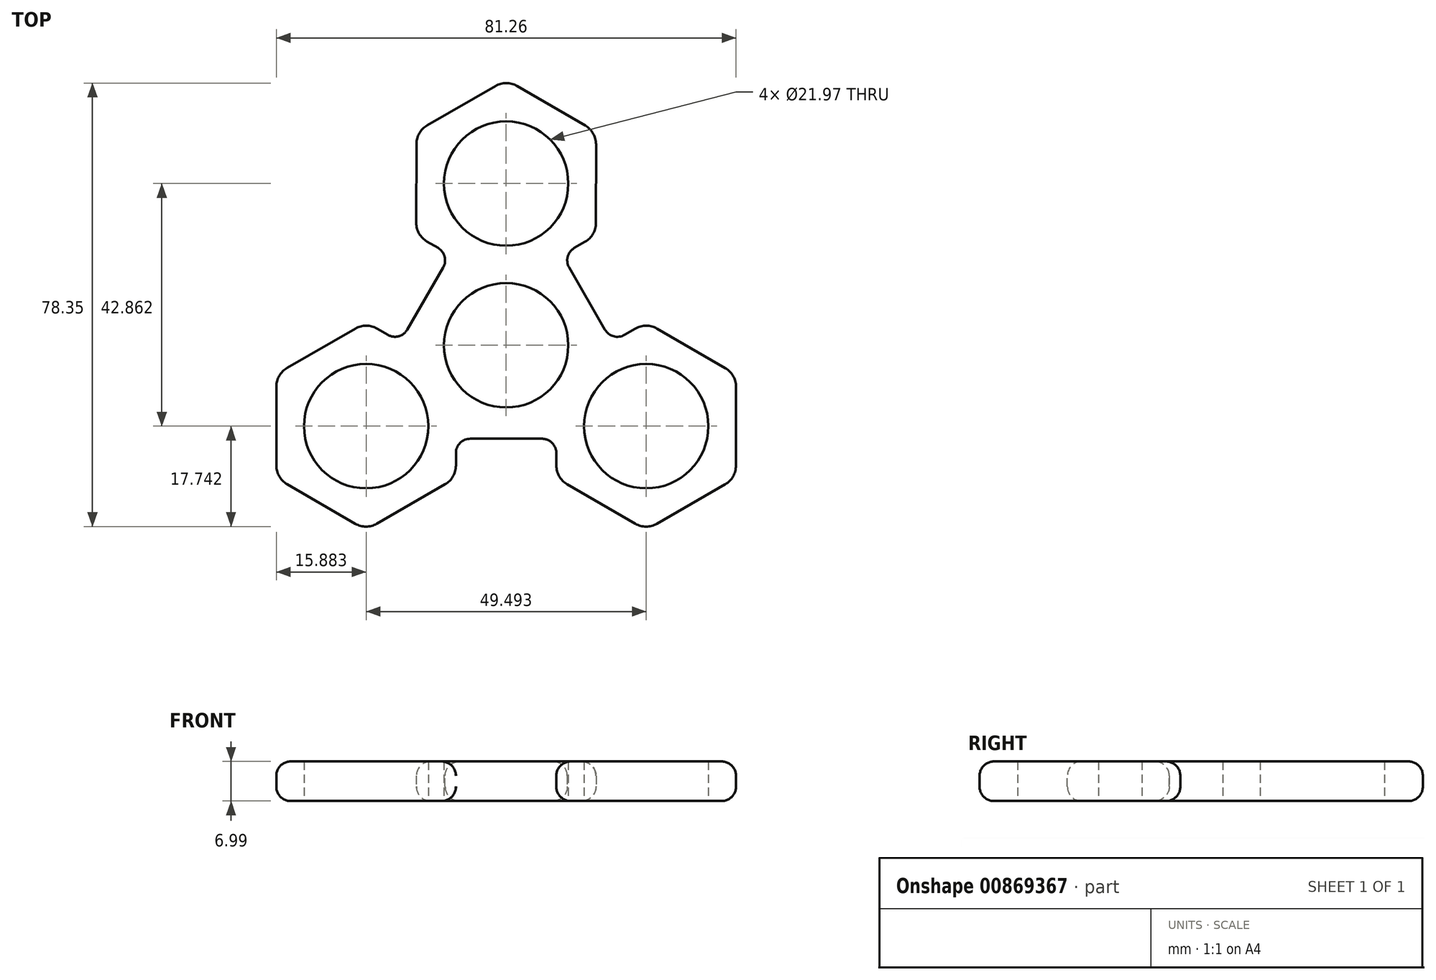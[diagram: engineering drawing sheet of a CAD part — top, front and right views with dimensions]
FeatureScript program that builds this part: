
annotation { "Feature Type Name" : "Feature", "Feature Type Description" : "" }
export const myFeature = defineFeature(function(context is Context, id is Id, definition is map)
    precondition{}
    {
        {
            var Q0;
            Q0=qCreatedBy(makeId("Top.planeOp"),FACE);
            var sketch = newSketch(context, id + "F0", { "sketchPlane" : qUnion([Q0])});
            skCircle(sketch, "E0", {"center": v(0, 0) * mm, "radius": 10.99 * mm});
            skCircle(sketch, "E1", {"center": v(0, 0) * mm, "radius": 4 * mm});
            skSolve(sketch);
        }
        {
            var Q0;
            Q0=qCreatedBy(makeId("Top.planeOp"),FACE);
            var sketch = newSketch(context, id + "F1", { "sketchPlane" : qUnion([Q0])});
            skCircle(sketch, "E2", {"center": v(0, 28.58) * mm, "radius": 10.99 * mm});
            skSolve(sketch);
        }
        {
            var Q0;
            Q0=qCreatedBy(makeId("Top.planeOp"),FACE);
            var sketch = newSketch(context, id + "F2", { "sketchPlane" : qUnion([Q0])});
            skCircle(sketch, "E3.cCircle", {"center": v(0, 28.58) * mm, "radius": 15.88 * mm, "construction": true});
            skLineSegment(sketch, "E3.0", {"start": v(-0.02, 10.24) * mm, "end": v(-15.88, 19.43) * mm});
            skLineSegment(sketch, "E3.1", {"start": v(-15.88, 19.43) * mm, "end": v(-15.87, 37.76) * mm});
            skLineSegment(sketch, "E3.2", {"start": v(-15.87, 37.76) * mm, "end": v(0.02, 46.9) * mm});
            skLineSegment(sketch, "E3.3", {"start": v(0.02, 46.9) * mm, "end": v(15.88, 37.72) * mm});
            skLineSegment(sketch, "E3.4", {"start": v(15.88, 37.72) * mm, "end": v(15.87, 19.4) * mm});
            skLineSegment(sketch, "E3.5", {"start": v(15.87, 19.4) * mm, "end": v(-0.02, 10.24) * mm});
            skPoint(sketch, "E3.0.midPoint", {"position": v(-7.95, 14.84) * mm});
            skCircle(sketch, "E4.0.0", {"center": v(0, 28.58) * mm, "radius": 10.99 * mm});
            skSolve(sketch);
        }
        {
            var Q0;
            Q0=makeQuery(id+"F1.imprint","IMPRINT",FACE,{"disambiguationData":[TD([[makeQuery(id+"F1.imprint","IMPRINT",EDGE,{"derivedFrom":sQuery(id+"F1.wireOp",EDGE,"E2")}),1.0]])]});
            var Q1;
            Q1=makeQuery(id+"F2.imprint","IMPRINT",FACE,{"disambiguationData":[TD([[makeQuery(id+"F2.imprint","IMPRINT",EDGE,{"derivedFrom":sQuery(id+"F2.wireOp",EDGE,"E3.0")}),-1.0]])]});
            extrude(context, id + "F3", {"entities" : qUnion([Q0, Q1]), "depth" : 7 * mm, "offsetDistance" : 25.4 * mm});
        }
        {
            var Q0;
            Q0=makeQuery(id+"F3.opExtrude","SWEPT_EDGE",EDGE,{"disambiguationData":[OSD([sQuery(id+"F2.wireOp",EDGE,"E3.0"),sQuery(id+"F2.wireOp",EDGE,"E3.5")])]});
            chamfer(context, id + "F4", {"entities" : qUnion([Q0]), "width" : 5.08 * mm, "tangentPropagation" : true});
        }
        {
            var Q0;
            Q0=makeQuery(id+"F3.opExtrude","SWEPT_BODY",BODY,{"disambiguationData":[OSD([sQuery(id+"F2.wireOp",EDGE,"E3.0"),sQuery(id+"F2.wireOp",EDGE,"E3.1"),sQuery(id+"F2.wireOp",EDGE,"E3.2"),sQuery(id+"F2.wireOp",EDGE,"E3.3"),sQuery(id+"F2.wireOp",EDGE,"E3.4"),sQuery(id+"F2.wireOp",EDGE,"E3.5"),sQuery(id+"F2.wireOp",EDGE,"E4.0.0")])]});
            var Q1;
            Q1=sQuery(id+"F0.wireOp",EDGE,"E1");
            circularPattern(context, id + "F5", {"entities" : qUnion([Q0]), "axis" : qUnion([Q1]), "angle" : 360 * degree, "instanceCount" : 3, "equalSpace" : true, "isCentered" : true});
        }
        {
            var Q0;
            Q0=qCreatedBy(makeId("Top.planeOp"),FACE);
            var sketch = newSketch(context, id + "F6", { "sketchPlane" : qUnion([Q0])});
            skCircle(sketch, "E5.cCircle", {"center": v(0, 0) * mm, "radius": 16.51 * mm, "construction": true});
            skLineSegment(sketch, "E5.0", {"start": v(9.53, -16.51) * mm, "end": v(-9.53, -16.51) * mm});
            skLineSegment(sketch, "E5.1", {"start": v(-9.53, -16.51) * mm, "end": v(-19.06, 0) * mm});
            skLineSegment(sketch, "E5.2", {"start": v(-19.06, 0) * mm, "end": v(-9.53, 16.51) * mm});
            skLineSegment(sketch, "E5.3", {"start": v(-9.53, 16.51) * mm, "end": v(9.53, 16.51) * mm});
            skLineSegment(sketch, "E5.4", {"start": v(9.53, 16.51) * mm, "end": v(19.06, 0) * mm});
            skLineSegment(sketch, "E5.5", {"start": v(19.06, 0) * mm, "end": v(9.53, -16.51) * mm});
            skPoint(sketch, "E5.0.midPoint", {"position": v(0, -16.51) * mm});
            skCircle(sketch, "E6", {"center": v(0, 0) * mm, "radius": 10.99 * mm});
            skSolve(sketch);
        }
        {
            var Q0;
            Q0=makeQuery(id+"F6.imprint","IMPRINT",FACE,{"disambiguationData":[TD([[makeQuery(id+"F6.imprint","IMPRINT",EDGE,{"derivedFrom":sQuery(id+"F6.wireOp",EDGE,"E5.0")}),-1.0]])]});
            var Q1;
            Q1=makeQuery(id+"F5.opPattern","COPY",FACE,{"derivedFrom":makeQuery(id+"F3.opExtrude","CAP_FACE",FACE,{"disambiguationData":[OSD([sQuery(id+"F2.wireOp",EDGE,"E3.0"),sQuery(id+"F2.wireOp",EDGE,"E3.1"),sQuery(id+"F2.wireOp",EDGE,"E3.2"),sQuery(id+"F2.wireOp",EDGE,"E3.3"),sQuery(id+"F2.wireOp",EDGE,"E3.4"),sQuery(id+"F2.wireOp",EDGE,"E3.5"),sQuery(id+"F2.wireOp",EDGE,"E4.0.0")])],"isStart":false}),"instanceName":"-2"});
            extrude(context, id + "F7", {"entities" : qUnion([Q0]), "operationType" : NewBodyOperationType.ADD, "endBound" : BoundingType.UP_TO_SURFACE, "depth" : 25.4 * mm, "endBoundEntityFace" : qUnion([Q1]), "offsetDistance" : 25.4 * mm});
        }
        {
            var Q0;
            Q0=makeQuery(id+"F5.opPattern","COPY",EDGE,{"derivedFrom":makeQuery(id+"F3.opExtrude","SWEPT_EDGE",EDGE,{"disambiguationData":[OSD([sQuery(id+"F2.wireOp",EDGE,"E3.1"),sQuery(id+"F2.wireOp",EDGE,"E3.2")])]}),"instanceName":"-2"});
            var Q1;
            Q1=makeQuery(id+"F5.opPattern","COPY",EDGE,{"derivedFrom":makeQuery(id+"F3.opExtrude","SWEPT_EDGE",EDGE,{"disambiguationData":[OSD([sQuery(id+"F2.wireOp",EDGE,"E3.0"),sQuery(id+"F2.wireOp",EDGE,"E3.1")])]}),"instanceName":"-2"});
            var Q2;
            Q2=makeQuery(id+"F5.opPattern","COPY",EDGE,{"derivedFrom":makeQuery(id+"F3.opExtrude","SWEPT_EDGE",EDGE,{"disambiguationData":[OSD([sQuery(id+"F2.wireOp",EDGE,"E3.4"),sQuery(id+"F2.wireOp",EDGE,"E3.5")])]}),"instanceName":"-1"});
            var Q3;
            Q3=makeQuery(id+"F5.opPattern","COPY",EDGE,{"derivedFrom":makeQuery(id+"F3.opExtrude","SWEPT_EDGE",EDGE,{"disambiguationData":[OSD([sQuery(id+"F2.wireOp",EDGE,"E3.3"),sQuery(id+"F2.wireOp",EDGE,"E3.4")])]}),"instanceName":"-1"});
            var Q4;
            Q4=makeQuery(id+"F5.opPattern","COPY",EDGE,{"derivedFrom":makeQuery(id+"F3.opExtrude","SWEPT_EDGE",EDGE,{"disambiguationData":[OSD([sQuery(id+"F2.wireOp",EDGE,"E3.2"),sQuery(id+"F2.wireOp",EDGE,"E3.3")])]}),"instanceName":"-1"});
            var Q5;
            Q5=makeQuery(id+"F5.opPattern","COPY",EDGE,{"derivedFrom":makeQuery(id+"F3.opExtrude","SWEPT_EDGE",EDGE,{"disambiguationData":[OSD([sQuery(id+"F2.wireOp",EDGE,"E3.1"),sQuery(id+"F2.wireOp",EDGE,"E3.2")])]}),"instanceName":"-1"});
            var Q6;
            Q6=makeQuery(id+"F5.opPattern","COPY",EDGE,{"derivedFrom":makeQuery(id+"F3.opExtrude","SWEPT_EDGE",EDGE,{"disambiguationData":[OSD([sQuery(id+"F2.wireOp",EDGE,"E3.0"),sQuery(id+"F2.wireOp",EDGE,"E3.1")])]}),"instanceName":"-1"});
            var Q7;
            Q7=makeQuery(id+"F3.opExtrude","SWEPT_EDGE",EDGE,{"disambiguationData":[OSD([sQuery(id+"F2.wireOp",EDGE,"E3.4"),sQuery(id+"F2.wireOp",EDGE,"E3.5")])]});
            var Q8;
            Q8=makeQuery(id+"F3.opExtrude","SWEPT_EDGE",EDGE,{"disambiguationData":[OSD([sQuery(id+"F2.wireOp",EDGE,"E3.3"),sQuery(id+"F2.wireOp",EDGE,"E3.4")])]});
            var Q9;
            Q9=makeQuery(id+"F3.opExtrude","SWEPT_EDGE",EDGE,{"disambiguationData":[OSD([sQuery(id+"F2.wireOp",EDGE,"E3.2"),sQuery(id+"F2.wireOp",EDGE,"E3.3")])]});
            var Q10;
            Q10=makeQuery(id+"F3.opExtrude","SWEPT_EDGE",EDGE,{"disambiguationData":[OSD([sQuery(id+"F2.wireOp",EDGE,"E3.1"),sQuery(id+"F2.wireOp",EDGE,"E3.2")])]});
            var Q11;
            Q11=makeQuery(id+"F3.opExtrude","SWEPT_EDGE",EDGE,{"disambiguationData":[OSD([sQuery(id+"F2.wireOp",EDGE,"E3.0"),sQuery(id+"F2.wireOp",EDGE,"E3.1")])]});
            var Q12;
            Q12=makeQuery(id+"F5.opPattern","COPY",EDGE,{"derivedFrom":makeQuery(id+"F3.opExtrude","SWEPT_EDGE",EDGE,{"disambiguationData":[OSD([sQuery(id+"F2.wireOp",EDGE,"E3.4"),sQuery(id+"F2.wireOp",EDGE,"E3.5")])]}),"instanceName":"-2"});
            var Q13;
            Q13=makeQuery(id+"F5.opPattern","COPY",EDGE,{"derivedFrom":makeQuery(id+"F3.opExtrude","SWEPT_EDGE",EDGE,{"disambiguationData":[OSD([sQuery(id+"F2.wireOp",EDGE,"E3.3"),sQuery(id+"F2.wireOp",EDGE,"E3.4")])]}),"instanceName":"-2"});
            var Q14;
            Q14=makeQuery(id+"F5.opPattern","COPY",EDGE,{"derivedFrom":makeQuery(id+"F3.opExtrude","SWEPT_EDGE",EDGE,{"disambiguationData":[OSD([sQuery(id+"F2.wireOp",EDGE,"E3.2"),sQuery(id+"F2.wireOp",EDGE,"E3.3")])]}),"instanceName":"-2"});
            fillet(context, id + "F8", {"entities" : qUnion([Q0, Q1, Q2, Q3, Q4, Q5, Q6, Q7, Q8, Q9, Q10, Q11, Q12, Q13, Q14]), "radius" : 3.8 * mm, "tangentPropagation" : true, "allowEdgeOverflow" : false});
        }
        {
            var Q0;
            Q0=makeQuery(id+"F7.boolean.opBoolean","INTERSECT",EDGE,{"derivedFrom":[makeQuery(id+"F3.opExtrude","SWEPT_FACE",FACE,{"disambiguationData":[OSD([sQuery(id+"F2.wireOp",EDGE,"E3.0")])]}),makeQuery(id+"F7.opExtrude","SWEPT_FACE",FACE,{"disambiguationData":[OSD([sQuery(id+"F6.wireOp",EDGE,"E5.2")])]})]});
            var Q1;
            {var subQ0=makeQuery(id+"F3.opExtrude","SWEPT_FACE",FACE,{"disambiguationData":[OSD([sQuery(id+"F2.wireOp",EDGE,"E3.5")])]});Q1=makeQuery(id+"F7.boolean.opBoolean","INTERSECT",EDGE,{"derivedFrom":[makeQuery(id+"F5.opPattern","COPY",FACE,{"derivedFrom":subQ0,"instanceName":"-2"}),makeQuery(id+"F5.opPattern","COPY",FACE,{"derivedFrom":subQ0,"instanceName":"1"}),makeQuery(id+"F7.opExtrude","SWEPT_FACE",FACE,{"disambiguationData":[OSD([sQuery(id+"F6.wireOp",EDGE,"E5.2")])]})]});}
            var Q2;
            {var subQ0=makeQuery(id+"F3.opExtrude","SWEPT_FACE",FACE,{"disambiguationData":[OSD([sQuery(id+"F2.wireOp",EDGE,"E3.0")])]});Q2=makeQuery(id+"F7.boolean.opBoolean","INTERSECT",EDGE,{"derivedFrom":[makeQuery(id+"F5.opPattern","COPY",FACE,{"derivedFrom":subQ0,"instanceName":"-2"}),makeQuery(id+"F5.opPattern","COPY",FACE,{"derivedFrom":subQ0,"instanceName":"1"}),makeQuery(id+"F7.opExtrude","SWEPT_FACE",FACE,{"disambiguationData":[OSD([sQuery(id+"F6.wireOp",EDGE,"E5.0")])]})]});}
            var Q3;
            {var subQ0=makeQuery(id+"F3.opExtrude","SWEPT_FACE",FACE,{"disambiguationData":[OSD([sQuery(id+"F2.wireOp",EDGE,"E3.5")])]});Q3=makeQuery(id+"F7.boolean.opBoolean","INTERSECT",EDGE,{"derivedFrom":[makeQuery(id+"F5.opPattern","COPY",FACE,{"derivedFrom":subQ0,"instanceName":"-1"}),makeQuery(id+"F5.opPattern","COPY",FACE,{"derivedFrom":subQ0,"instanceName":"2"}),makeQuery(id+"F7.opExtrude","SWEPT_FACE",FACE,{"disambiguationData":[OSD([sQuery(id+"F6.wireOp",EDGE,"E5.0")])]})]});}
            var Q4;
            Q4=makeQuery(id+"F7.boolean.opBoolean","INTERSECT",EDGE,{"derivedFrom":[makeQuery(id+"F3.opExtrude","SWEPT_FACE",FACE,{"disambiguationData":[OSD([sQuery(id+"F2.wireOp",EDGE,"E3.5")])]}),makeQuery(id+"F7.opExtrude","SWEPT_FACE",FACE,{"disambiguationData":[OSD([sQuery(id+"F6.wireOp",EDGE,"E5.4")])]})]});
            var Q5;
            {var subQ0=makeQuery(id+"F3.opExtrude","SWEPT_FACE",FACE,{"disambiguationData":[OSD([sQuery(id+"F2.wireOp",EDGE,"E3.0")])]});Q5=makeQuery(id+"F7.boolean.opBoolean","INTERSECT",EDGE,{"derivedFrom":[makeQuery(id+"F5.opPattern","COPY",FACE,{"derivedFrom":subQ0,"instanceName":"-1"}),makeQuery(id+"F5.opPattern","COPY",FACE,{"derivedFrom":subQ0,"instanceName":"2"}),makeQuery(id+"F7.opExtrude","SWEPT_FACE",FACE,{"disambiguationData":[OSD([sQuery(id+"F6.wireOp",EDGE,"E5.4")])]})]});}
            fillet(context, id + "F9", {"entities" : qUnion([Q0, Q1, Q2, Q3, Q4, Q5]), "radius" : 2.54 * mm, "tangentPropagation" : true, "allowEdgeOverflow" : false});
        }
        {
            var Q0;
            Q0=makeQuery(id+"F7.opExtrude","TWEAK_EDGE",EDGE,{"derivedFrom":[makeQuery(id+"F5.opPattern","COPY",FACE,{"derivedFrom":makeQuery(id+"F3.opExtrude","CAP_FACE",FACE,{"disambiguationData":[OSD([sQuery(id+"F2.wireOp",EDGE,"E3.0"),sQuery(id+"F2.wireOp",EDGE,"E3.1"),sQuery(id+"F2.wireOp",EDGE,"E3.2"),sQuery(id+"F2.wireOp",EDGE,"E3.3"),sQuery(id+"F2.wireOp",EDGE,"E3.4"),sQuery(id+"F2.wireOp",EDGE,"E3.5"),sQuery(id+"F2.wireOp",EDGE,"E4.0.0")])],"isStart":false}),"instanceName":"-2"}),makeQuery(id+"F6.imprint","IMPRINT",EDGE,{"derivedFrom":sQuery(id+"F6.wireOp",EDGE,"E5.2")})]});
            var Q1;
            Q1=makeQuery(id+"F7.opExtrude","CAP_EDGE",EDGE,{"disambiguationData":[OSD([sQuery(id+"F6.wireOp",EDGE,"E5.2")])],"isStart":true});
            var Q2;
            Q2=makeQuery(id+"F7.opExtrude","TWEAK_EDGE",EDGE,{"derivedFrom":[makeQuery(id+"F5.opPattern","COPY",FACE,{"derivedFrom":makeQuery(id+"F3.opExtrude","CAP_FACE",FACE,{"disambiguationData":[OSD([sQuery(id+"F2.wireOp",EDGE,"E3.0"),sQuery(id+"F2.wireOp",EDGE,"E3.1"),sQuery(id+"F2.wireOp",EDGE,"E3.2"),sQuery(id+"F2.wireOp",EDGE,"E3.3"),sQuery(id+"F2.wireOp",EDGE,"E3.4"),sQuery(id+"F2.wireOp",EDGE,"E3.5"),sQuery(id+"F2.wireOp",EDGE,"E4.0.0")])],"isStart":false}),"instanceName":"-2"}),makeQuery(id+"F6.imprint","IMPRINT",EDGE,{"derivedFrom":sQuery(id+"F6.wireOp",EDGE,"E5.4")})]});
            var Q3;
            Q3=makeQuery(id+"F7.opExtrude","TWEAK_EDGE",EDGE,{"derivedFrom":[makeQuery(id+"F5.opPattern","COPY",FACE,{"derivedFrom":makeQuery(id+"F3.opExtrude","CAP_FACE",FACE,{"disambiguationData":[OSD([sQuery(id+"F2.wireOp",EDGE,"E3.0"),sQuery(id+"F2.wireOp",EDGE,"E3.1"),sQuery(id+"F2.wireOp",EDGE,"E3.2"),sQuery(id+"F2.wireOp",EDGE,"E3.3"),sQuery(id+"F2.wireOp",EDGE,"E3.4"),sQuery(id+"F2.wireOp",EDGE,"E3.5"),sQuery(id+"F2.wireOp",EDGE,"E4.0.0")])],"isStart":false}),"instanceName":"-2"}),makeQuery(id+"F6.imprint","IMPRINT",EDGE,{"derivedFrom":sQuery(id+"F6.wireOp",EDGE,"E5.0")})]});
            var Q4;
            Q4=makeQuery(id+"F7.opExtrude","CAP_EDGE",EDGE,{"disambiguationData":[OSD([sQuery(id+"F6.wireOp",EDGE,"E5.0")])],"isStart":true});
            var Q5;
            Q5=makeQuery(id+"F7.opExtrude","CAP_EDGE",EDGE,{"disambiguationData":[OSD([sQuery(id+"F6.wireOp",EDGE,"E5.4")])],"isStart":true});
            fillet(context, id + "F10", {"entities" : qUnion([Q0, Q1, Q2, Q3, Q4, Q5]), "radius" : 2.54 * mm, "tangentPropagation" : true, "allowEdgeOverflow" : false});
        }
        {
            var Q0;
            Q0=makeQuery(id+"F5.opPattern","COPY",EDGE,{"derivedFrom":makeQuery(id+"F3.opExtrude","CAP_EDGE",EDGE,{"disambiguationData":[OSD([sQuery(id+"F2.wireOp",EDGE,"E3.1")])],"isStart":false}),"instanceName":"-2"});
            var Q1;
            Q1=makeQuery(id+"F5.opPattern","COPY",EDGE,{"derivedFrom":makeQuery(id+"F3.opExtrude","CAP_EDGE",EDGE,{"disambiguationData":[OSD([sQuery(id+"F2.wireOp",EDGE,"E3.3")])],"isStart":false}),"instanceName":"-2"});
            var Q2;
            Q2=makeQuery(id+"F5.opPattern","COPY",EDGE,{"derivedFrom":makeQuery(id+"F3.opExtrude","CAP_EDGE",EDGE,{"disambiguationData":[OSD([sQuery(id+"F2.wireOp",EDGE,"E3.2")])],"isStart":false}),"instanceName":"-2"});
            var Q3;
            Q3=makeQuery(id+"F5.opPattern","COPY",EDGE,{"derivedFrom":makeQuery(id+"F3.opExtrude","CAP_EDGE",EDGE,{"disambiguationData":[OSD([sQuery(id+"F2.wireOp",EDGE,"E3.4")])],"isStart":false}),"instanceName":"-2"});
            var Q4;
            Q4=makeQuery(id+"F5.opPattern","COPY",EDGE,{"derivedFrom":makeQuery(id+"F3.opExtrude","CAP_EDGE",EDGE,{"disambiguationData":[OSD([sQuery(id+"F2.wireOp",EDGE,"E3.5")])],"isStart":false}),"instanceName":"-2"});
            var Q5;
            Q5=makeQuery(id+"F3.opExtrude","CAP_EDGE",EDGE,{"disambiguationData":[OSD([sQuery(id+"F2.wireOp",EDGE,"E3.0")])],"isStart":false});
            var Q6;
            Q6=makeQuery(id+"F3.opExtrude","CAP_EDGE",EDGE,{"disambiguationData":[OSD([sQuery(id+"F2.wireOp",EDGE,"E3.1")])],"isStart":false});
            var Q7;
            Q7=makeQuery(id+"F3.opExtrude","CAP_EDGE",EDGE,{"disambiguationData":[OSD([sQuery(id+"F2.wireOp",EDGE,"E3.2")])],"isStart":false});
            var Q8;
            Q8=makeQuery(id+"F5.opPattern","COPY",EDGE,{"derivedFrom":makeQuery(id+"F3.opExtrude","CAP_EDGE",EDGE,{"disambiguationData":[OSD([sQuery(id+"F2.wireOp",EDGE,"E3.5")])],"isStart":false}),"instanceName":"-1"});
            var Q9;
            Q9=makeQuery(id+"F5.opPattern","COPY",EDGE,{"derivedFrom":makeQuery(id+"F3.opExtrude","CAP_EDGE",EDGE,{"disambiguationData":[OSD([sQuery(id+"F2.wireOp",EDGE,"E3.4")])],"isStart":false}),"instanceName":"-1"});
            var Q10;
            Q10=makeQuery(id+"F5.opPattern","COPY",EDGE,{"derivedFrom":makeQuery(id+"F3.opExtrude","CAP_EDGE",EDGE,{"disambiguationData":[OSD([sQuery(id+"F2.wireOp",EDGE,"E3.3")])],"isStart":false}),"instanceName":"-1"});
            var Q11;
            Q11=makeQuery(id+"F5.opPattern","COPY",EDGE,{"derivedFrom":makeQuery(id+"F3.opExtrude","CAP_EDGE",EDGE,{"disambiguationData":[OSD([sQuery(id+"F2.wireOp",EDGE,"E3.2")])],"isStart":false}),"instanceName":"-1"});
            var Q12;
            Q12=makeQuery(id+"F5.opPattern","COPY",EDGE,{"derivedFrom":makeQuery(id+"F3.opExtrude","CAP_EDGE",EDGE,{"disambiguationData":[OSD([sQuery(id+"F2.wireOp",EDGE,"E3.1")])],"isStart":false}),"instanceName":"-1"});
            var Q13;
            Q13=makeQuery(id+"F5.opPattern","COPY",EDGE,{"derivedFrom":makeQuery(id+"F3.opExtrude","CAP_EDGE",EDGE,{"disambiguationData":[OSD([sQuery(id+"F2.wireOp",EDGE,"E3.0")])],"isStart":false}),"instanceName":"-1"});
            var Q14;
            Q14=makeQuery(id+"F3.opExtrude","CAP_EDGE",EDGE,{"disambiguationData":[OSD([sQuery(id+"F2.wireOp",EDGE,"E3.5")])],"isStart":false});
            var Q15;
            Q15=makeQuery(id+"F3.opExtrude","CAP_EDGE",EDGE,{"disambiguationData":[OSD([sQuery(id+"F2.wireOp",EDGE,"E3.4")])],"isStart":false});
            var Q16;
            Q16=makeQuery(id+"F3.opExtrude","CAP_EDGE",EDGE,{"disambiguationData":[OSD([sQuery(id+"F2.wireOp",EDGE,"E3.3")])],"isStart":false});
            var Q17;
            Q17=makeQuery(id+"F5.opPattern","COPY",EDGE,{"derivedFrom":makeQuery(id+"F3.opExtrude","CAP_EDGE",EDGE,{"disambiguationData":[OSD([sQuery(id+"F2.wireOp",EDGE,"E3.0")])],"isStart":true}),"instanceName":"-2"});
            var Q18;
            Q18=makeQuery(id+"F5.opPattern","COPY",EDGE,{"derivedFrom":makeQuery(id+"F3.opExtrude","CAP_EDGE",EDGE,{"disambiguationData":[OSD([sQuery(id+"F2.wireOp",EDGE,"E3.1")])],"isStart":true}),"instanceName":"-2"});
            var Q19;
            Q19=makeQuery(id+"F5.opPattern","COPY",EDGE,{"derivedFrom":makeQuery(id+"F3.opExtrude","CAP_EDGE",EDGE,{"disambiguationData":[OSD([sQuery(id+"F2.wireOp",EDGE,"E3.4")])],"isStart":true}),"instanceName":"-2"});
            var Q20;
            Q20=makeQuery(id+"F5.opPattern","COPY",EDGE,{"derivedFrom":makeQuery(id+"F3.opExtrude","CAP_EDGE",EDGE,{"disambiguationData":[OSD([sQuery(id+"F2.wireOp",EDGE,"E3.3")])],"isStart":true}),"instanceName":"-2"});
            var Q21;
            Q21=makeQuery(id+"F5.opPattern","COPY",EDGE,{"derivedFrom":makeQuery(id+"F3.opExtrude","CAP_EDGE",EDGE,{"disambiguationData":[OSD([sQuery(id+"F2.wireOp",EDGE,"E3.2")])],"isStart":true}),"instanceName":"-2"});
            var Q22;
            Q22=makeQuery(id+"F5.opPattern","COPY",EDGE,{"derivedFrom":makeQuery(id+"F3.opExtrude","CAP_EDGE",EDGE,{"disambiguationData":[OSD([sQuery(id+"F2.wireOp",EDGE,"E3.5")])],"isStart":true}),"instanceName":"-2"});
            var Q23;
            Q23=makeQuery(id+"F3.opExtrude","CAP_EDGE",EDGE,{"disambiguationData":[OSD([sQuery(id+"F2.wireOp",EDGE,"E3.0")])],"isStart":true});
            var Q24;
            Q24=makeQuery(id+"F3.opExtrude","CAP_EDGE",EDGE,{"disambiguationData":[OSD([sQuery(id+"F2.wireOp",EDGE,"E3.1")])],"isStart":true});
            var Q25;
            Q25=makeQuery(id+"F3.opExtrude","CAP_EDGE",EDGE,{"disambiguationData":[OSD([sQuery(id+"F2.wireOp",EDGE,"E3.2")])],"isStart":true});
            var Q26;
            Q26=makeQuery(id+"F3.opExtrude","CAP_EDGE",EDGE,{"disambiguationData":[OSD([sQuery(id+"F2.wireOp",EDGE,"E3.3")])],"isStart":true});
            var Q27;
            Q27=makeQuery(id+"F3.opExtrude","CAP_EDGE",EDGE,{"disambiguationData":[OSD([sQuery(id+"F2.wireOp",EDGE,"E3.4")])],"isStart":true});
            var Q28;
            Q28=makeQuery(id+"F3.opExtrude","CAP_EDGE",EDGE,{"disambiguationData":[OSD([sQuery(id+"F2.wireOp",EDGE,"E3.5")])],"isStart":true});
            var Q29;
            Q29=makeQuery(id+"F5.opPattern","COPY",EDGE,{"derivedFrom":makeQuery(id+"F3.opExtrude","CAP_EDGE",EDGE,{"disambiguationData":[OSD([sQuery(id+"F2.wireOp",EDGE,"E3.0")])],"isStart":true}),"instanceName":"-1"});
            var Q30;
            Q30=makeQuery(id+"F5.opPattern","COPY",EDGE,{"derivedFrom":makeQuery(id+"F3.opExtrude","CAP_EDGE",EDGE,{"disambiguationData":[OSD([sQuery(id+"F2.wireOp",EDGE,"E3.1")])],"isStart":true}),"instanceName":"-1"});
            var Q31;
            Q31=makeQuery(id+"F5.opPattern","COPY",EDGE,{"derivedFrom":makeQuery(id+"F3.opExtrude","CAP_EDGE",EDGE,{"disambiguationData":[OSD([sQuery(id+"F2.wireOp",EDGE,"E3.3")])],"isStart":true}),"instanceName":"-1"});
            var Q32;
            Q32=makeQuery(id+"F5.opPattern","COPY",EDGE,{"derivedFrom":makeQuery(id+"F3.opExtrude","CAP_EDGE",EDGE,{"disambiguationData":[OSD([sQuery(id+"F2.wireOp",EDGE,"E3.4")])],"isStart":true}),"instanceName":"-1"});
            var Q33;
            Q33=makeQuery(id+"F5.opPattern","COPY",EDGE,{"derivedFrom":makeQuery(id+"F3.opExtrude","CAP_EDGE",EDGE,{"disambiguationData":[OSD([sQuery(id+"F2.wireOp",EDGE,"E3.5")])],"isStart":true}),"instanceName":"-1"});
            var Q34;
            Q34=makeQuery(id+"F5.opPattern","COPY",EDGE,{"derivedFrom":makeQuery(id+"F3.opExtrude","CAP_EDGE",EDGE,{"disambiguationData":[OSD([sQuery(id+"F2.wireOp",EDGE,"E3.2")])],"isStart":true}),"instanceName":"-1"});
            var Q35;
            Q35=makeQuery(id+"F5.opPattern","COPY",EDGE,{"derivedFrom":makeQuery(id+"F3.opExtrude","CAP_EDGE",EDGE,{"disambiguationData":[OSD([sQuery(id+"F2.wireOp",EDGE,"E3.0")])],"isStart":false}),"instanceName":"-2"});
            fillet(context, id + "F11", {"entities" : qUnion([Q0, Q1, Q2, Q3, Q4, Q5, Q6, Q7, Q8, Q9, Q10, Q11, Q12, Q13, Q14, Q15, Q16, Q17, Q18, Q19, Q20, Q21, Q22, Q23, Q24, Q25, Q26, Q27, Q28, Q29, Q30, Q31, Q32, Q33, Q34, Q35]), "radius" : 2.54 * mm, "tangentPropagation" : true, "allowEdgeOverflow" : false});
        }
    });
